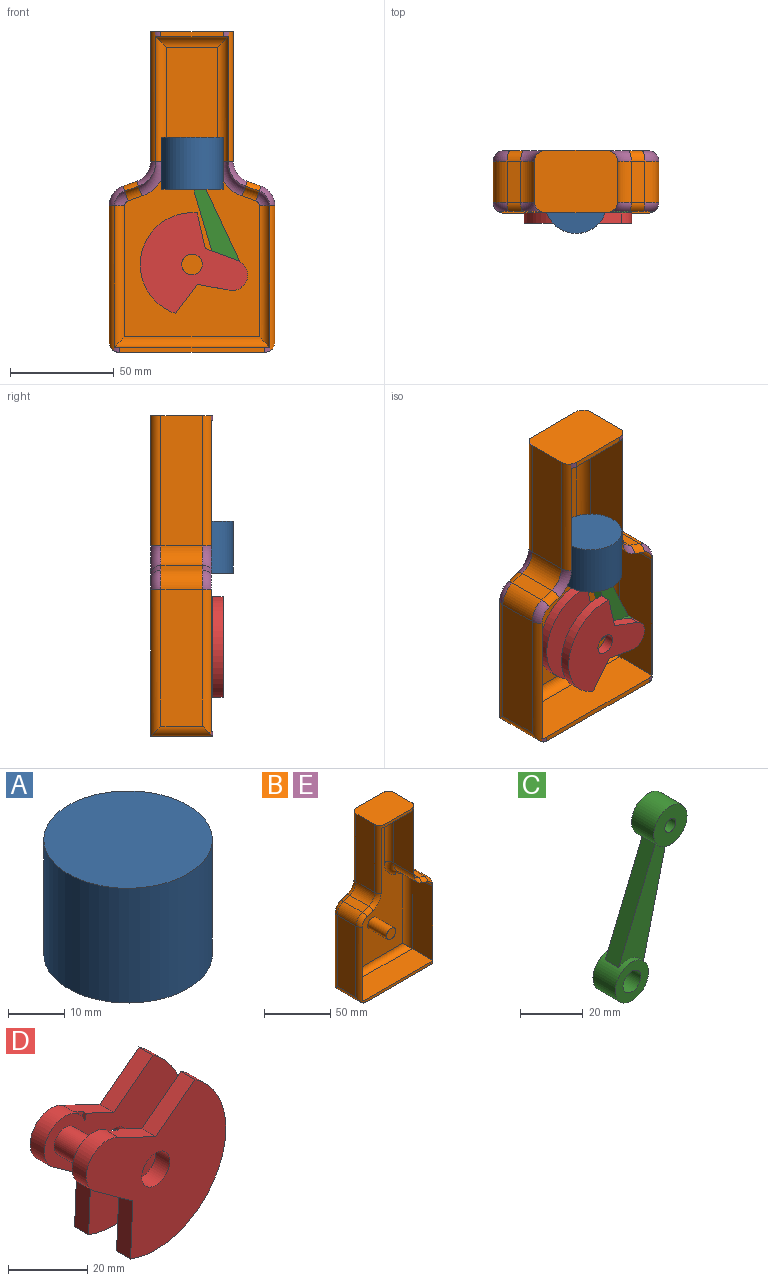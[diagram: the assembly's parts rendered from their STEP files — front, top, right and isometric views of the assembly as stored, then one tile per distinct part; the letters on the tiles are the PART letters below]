
ASSEMBLY  parts=5 mates=4
PART A: 17 faces, bbox 30x30x25 mm
  f0: cylinder r=5mm len=10mm, axis (0,1,0), area 101.5mm2, adj f1,f3,f8,f11
  f1: plane 21.82x12mm, normal (1,0,0), area 181.8mm2, adj f0,f3,f7,f9,f10,f11,f12
  f2: plane 21.82x7mm, normal (0,0,-1), area 109.8mm2, adj f3,f8
  f3: cylinder r=12mm len=24mm, axis (0,0,1), area 1330.9mm2, adj f0,f1,f2,f5,f7,f8,f9
  f4: plane 30x30mm, normal (0,0,1), area 706.9mm2, adj f6
  f5: plane 30x30mm, normal (0,0,-1), area 254.5mm2, adj f3,f6
  f6: cylinder r=15mm len=30mm, axis (0,0,1), area 2356.2mm2, adj f4,f5
  f7: plane 21.82x7mm, normal (0,0,-1), area 109.8mm2, adj f1,f3
  f8: plane 21.82x12mm, normal (-1,0,0), area 181.8mm2, adj f0,f2,f3,f9,f10,f11,f12
  f9: cylinder r=5mm len=10mm, axis (0,1,0), area 101.5mm2, adj f1,f3,f8,f12
  f10: plane 10x10mm, normal (0,0,-1), area 100mm2, adj f1,f8,f11,f12
  f11: plane 13x10mm, normal (0,-1,0), area 99.6mm2, adj f0,f1,f8,f10,f15
  f12: plane 13x10mm, normal (0,1,0), area 99.6mm2, adj f1,f8,f9,f10,f14
  f13: cylinder r=12mm len=5mm, axis (0,0,1), area 19.7mm2, adj f14
  f14: cylinder r=2.5mm len=7mm, axis (0,1,0), area 107.9mm2, adj f12,f13
  f15: cylinder r=2.5mm len=7mm, axis (0,1,0), area 107.9mm2, adj f11,f16
  f16: cylinder r=12mm len=5mm, axis (0,0,1), area 19.7mm2, adj f15
PART B: 64 faces, bbox 81.6x30x155 mm
  f0: plane 30x2.5mm, normal (0,-1,0), area 75mm2, adj f9,f23,f28,f39
  f1: cylinder r=10mm len=20mm, axis (0,1,0), area 246.5mm2, adj f2,f12,f42,f46
  f2: plane 65.88x20mm, normal (-1,0,0), area 1317.6mm2, adj f1,f43,f44,f45
  f3: plane 70x30mm, normal (0,0,-1), area 2100mm2, adj f13,f14,f33,f44
  f4: plane 65.88x20mm, normal (1,0,0), area 1317.6mm2, adj f5,f32,f33,f34
  f5: cylinder r=10mm len=20mm, axis (0,1,0), area 246.5mm2, adj f4,f6,f31,f35
  f6: plane 20x6.64mm, normal (0.33,0,0.94), area 140.7mm2, adj f5,f7,f30,f36
  f7: cylinder r=10mm len=20mm, axis (0,1,0), area 246.5mm2, adj f6,f8,f29,f37
  f8: plane 62.92x20mm, normal (1,0,0), area 1258.3mm2, adj f7,f9,f28,f38
  f9: plane 40x30mm, normal (0,0,1), area 1178.5mm2, adj f0,f8,f10,f14,f28,f38,f39,f49
  f10: plane 62.92x20mm, normal (-1,0,0), area 1258.3mm2, adj f9,f11,f39,f49
  f11: cylinder r=10mm len=20mm, axis (0,1,0), area 246.5mm2, adj f10,f12,f40,f48
  f12: plane 20x6.64mm, normal (-0.33,0,0.94), area 140.7mm2, adj f1,f11,f41,f47
  f13: plane 70x2.5mm, normal (0,-1,0), area 175mm2, adj f3,f17,f32,f43
  f14: plane 155x70mm, normal (0,1,0), area 7804.5mm2, adj f3,f9,f34,f35,f36,f37,f38,f45
  f15: cylinder r=7.5mm len=21.83mm, axis (0,1,0), area 201.8mm2, adj f16,f26,f42,f58
  f16: plane 68.38x21.83mm, normal (1,0,0), area 1492.8mm2, adj f15,f17,f43,f60
  f17: plane 75x22.5mm, normal (0,0,1), area 1686.4mm2, adj f13,f16,f18,f32,f43,f62
  f18: plane 68.38x21.83mm, normal (-1,0,0), area 1492.8mm2, adj f17,f19,f32,f63
  f19: cylinder r=7.5mm len=21.83mm, axis (0,1,0), area 201.8mm2, adj f18,f20,f31,f61
  f20: plane 21.83x6.64mm, normal (-0.33,0,-0.94), area 153.6mm2, adj f19,f21,f30,f59
  f21: cylinder r=12.5mm len=21.83mm, axis (0,1,0), area 336.3mm2, adj f20,f22,f29,f57
  f22: plane 60.42x21.83mm, normal (-1,0,0), area 1318.9mm2, adj f21,f23,f28,f55
  f23: plane 35x22.5mm, normal (0,0,-1), area 786.4mm2, adj f0,f22,f24,f28,f39,f53
  f24: plane 60.42x21.83mm, normal (1,0,0), area 1318.9mm2, adj f23,f25,f39,f52
  f25: cylinder r=12.5mm len=21.83mm, axis (0,1,0), area 336.3mm2, adj f24,f26,f40,f54
  f26: plane 21.83x6.64mm, normal (0.33,0,-0.94), area 153.6mm2, adj f15,f25,f41,f56
  f27: plane 140x65mm, normal (0,-1,0), area 6223.5mm2, adj f50,f52,f53,f54,f55,f56,f57,f58
  f28: cylinder r=5mm len=62.92mm, axis (0,0,-1), area 336mm2, adj f0,f8,f9,f22,f23,f29
  f29: torus R=15mm, axis (0,-1,0), area 70.1mm2, adj f7,f21,f28,f30
  f30: cylinder r=5mm len=7.47mm, axis (0.94,0,-0.33), area 36.8mm2, adj f6,f20,f29,f31
  f31: torus R=5mm, axis (0,-1,0), area 59mm2, adj f5,f19,f30,f32
  f32: cylinder r=5mm len=70.88mm, axis (0,0,-1), area 363.4mm2, adj f4,f13,f17,f18,f31,f33
  f33: cylinder r=5mm len=30mm, axis (0,-1,0), area 207.1mm2, adj f3,f4,f32,f34
  f34: cylinder r=5mm len=70.88mm, axis (0,0,1), area 542.4mm2, adj f4,f14,f33,f35
  f35: torus R=5mm, axis (0,-1,0), area 79.2mm2, adj f5,f14,f34,f36
  f36: cylinder r=5mm len=8.29mm, axis (-0.94,0,0.33), area 55.2mm2, adj f6,f14,f35,f37
  f37: torus R=15mm, axis (0,-1,0), area 114.4mm2, adj f7,f14,f36,f38
  f38: cylinder r=5mm len=62.92mm, axis (0,0,1), area 494.1mm2, adj f8,f9,f14,f37
  f39: cylinder r=5mm len=62.92mm, axis (0,0,1), area 336mm2, adj f0,f9,f10,f23,f24,f40
  f40: torus R=15mm, axis (0,-1,0), area 70.1mm2, adj f11,f25,f39,f41
  f41: cylinder r=5mm len=7.47mm, axis (-0.94,0,-0.33), area 36.8mm2, adj f12,f26,f40,f42
  f42: torus R=5mm, axis (0,-1,0), area 59mm2, adj f1,f15,f41,f43
  f43: cylinder r=5mm len=70.88mm, axis (0,0,1), area 363.4mm2, adj f2,f13,f16,f17,f42,f44
  f44: cylinder r=5mm len=30mm, axis (0,1,0), area 207.1mm2, adj f2,f3,f43,f45
  f45: cylinder r=5mm len=70.88mm, axis (0,0,-1), area 542.4mm2, adj f2,f14,f44,f46
  f46: torus R=5mm, axis (0,-1,0), area 79.2mm2, adj f1,f14,f45,f47
  f47: cylinder r=5mm len=8.29mm, axis (-0.94,0,-0.33), area 55.2mm2, adj f12,f14,f46,f48
  f48: torus R=15mm, axis (0,-1,0), area 114.4mm2, adj f11,f14,f47,f49
  f49: cylinder r=5mm len=62.92mm, axis (0,0,-1), area 494.1mm2, adj f9,f10,f14,f48
  f50: cylinder r=5mm len=20mm, axis (0,-1,0), area 628.3mm2, adj f27,f51
  f51: plane 10x10mm, normal (0,-1,0), area 78.5mm2, adj f50
  f52: cylinder r=5mm len=60.42mm, axis (0,0,1), area 460.2mm2, adj f24,f27,f53,f54
  f53: cylinder r=5mm len=35mm, axis (1,0,0), area 246.3mm2, adj f23,f27,f52,f55
  f54: torus R=17.5mm, axis (0,-1,0), area 138.6mm2, adj f25,f27,f52,f56
  f55: cylinder r=5mm len=60.42mm, axis (0,0,-1), area 460.2mm2, adj f22,f27,f53,f57
  f56: cylinder r=5mm len=8.29mm, axis (0.94,0,0.33), area 55.2mm2, adj f26,f27,f54,f58
  f57: torus R=17.5mm, axis (0,-1,0), area 138.6mm2, adj f21,f27,f55,f59
  f58: torus R=2.5mm, axis (0,-1,0), area 55mm2, adj f15,f27,f56,f60
  f59: cylinder r=5mm len=8.29mm, axis (0.94,0,-0.33), area 55.2mm2, adj f20,f27,f57,f61
  f60: cylinder r=5mm len=68.38mm, axis (0,0,1), area 522.8mm2, adj f16,f27,f58,f62
  f61: torus R=2.5mm, axis (0,-1,0), area 55mm2, adj f19,f27,f59,f63
  f62: cylinder r=5mm len=75mm, axis (-1,0,0), area 560.5mm2, adj f17,f27,f60,f63
  f63: cylinder r=5mm len=68.38mm, axis (0,0,-1), area 522.8mm2, adj f18,f27,f61,f62
PART C: 12 faces, bbox 32.3x10x67.2 mm
  f0: plane 39.99x16.56mm, normal (-0.92,0,0.38), area 259.7mm2, adj f8,f9,f10,f11
  f1: plane 42.04x10.31mm, normal (0.97,0,-0.24), area 259.7mm2, adj f8,f9,f10,f11
  f2: plane 15x15mm, normal (0,-1,0), area 157.1mm2, adj f7,f9
  f3: plane 15x15mm, normal (0,-1,0), area 126.4mm2, adj f6,f8
  f4: plane 15x15mm, normal (0,1,0), area 157.1mm2, adj f7,f9
  f5: plane 15x15mm, normal (0,1,0), area 126.4mm2, adj f6,f8
  f6: cylinder r=4mm len=10mm, axis (0,1,0), area 251.3mm2, adj f3,f5
  f7: cylinder r=2.5mm len=10mm, axis (0,1,0), area 157.1mm2, adj f2,f4
  f8: cylinder r=7.5mm len=15mm, axis (0,1,0), area 391.9mm2, adj f0,f1,f3,f5,f10,f11
  f9: cylinder r=7.5mm len=15mm, axis (0,1,0), area 440.7mm2, adj f0,f1,f2,f4,f10,f11
  f10: plane 43.71x21.27mm, normal (0,1,0), area 334.2mm2, adj f0,f1,f8,f9
  f11: plane 43.71x21.27mm, normal (0,-1,0), area 334.2mm2, adj f0,f1,f8,f9
PART D: 23 faces, bbox 49.8x20x45.7 mm
  f0: plane 49.82x45.72mm, normal (0,1,0), area 1300.3mm2, adj f10,f11,f12,f13,f14,f15,f16,f18
  f1: plane 49.82x45.72mm, normal (0,-1,0), area 1300.3mm2, adj f2,f3,f4,f5,f6,f7,f8,f18
  f2: plane 13.29x6.32mm, normal (0.43,0,0.9), area 69.7mm2, adj f1,f3,f4,f9,f19,f20
  f3: plane 13.98x10.72mm, normal (-0.61,0,0.79), area 88.1mm2, adj f1,f2,f8,f9
  f4: cylinder r=7.5mm len=14.51mm, axis (0,-1,0), area 120.7mm2, adj f1,f2,f5,f9,f19,f20
  f5: plane 13.48x9.63mm, normal (-0.58,0,-0.81), area 82.8mm2, adj f1,f4,f6,f9
  f6: plane 17.61x5mm, normal (-1,0,0.04), area 88.1mm2, adj f1,f5,f8,f9
  f7: cylinder r=5mm len=10mm, axis (0,-1,0), area 157.1mm2, adj f1,f9
  f8: cylinder r=25mm len=45.72mm, axis (0,-1,0), area 364.4mm2, adj f1,f3,f6,f9
  f9: plane 49.82x45.72mm, normal (0,1,0), area 1353.2mm2, adj f2,f3,f4,f5,f6,f7,f8
  f10: plane 13.98x10.72mm, normal (-0.61,0,0.79), area 88.1mm2, adj f0,f11,f16,f17
  f11: plane 13.29x6.32mm, normal (0.43,0,0.9), area 69.7mm2, adj f0,f10,f12,f17,f21,f22
  f12: cylinder r=7.5mm len=14.51mm, axis (0,1,0), area 120.7mm2, adj f0,f11,f13,f17,f21,f22
  f13: plane 13.48x9.63mm, normal (-0.58,0,-0.81), area 82.8mm2, adj f0,f12,f14,f17
  f14: plane 17.61x5mm, normal (-1,0,0.04), area 88.1mm2, adj f0,f13,f16,f17
  f15: cylinder r=5mm len=10mm, axis (0,1,0), area 157.1mm2, adj f0,f17
  f16: cylinder r=25mm len=45.72mm, axis (0,1,0), area 364.4mm2, adj f0,f10,f14,f17
  f17: plane 49.82x45.72mm, normal (0,-1,0), area 1353.2mm2, adj f10,f11,f12,f13,f14,f15,f16
  f18: cylinder r=4mm len=10mm, axis (0,1,0), area 251.3mm2, adj f0,f1
  f19: plane 3.66x3.47mm, normal (0,-1,0), area 2.7mm2, adj f2,f4,f20
  f20: plane 2.01x1mm, normal (-0.97,0,0.24), area 2.1mm2, adj f1,f2,f4,f19
  f21: plane 2.01x1mm, normal (-0.97,0,0.24), area 2.1mm2, adj f0,f11,f12,f22
  f22: plane 3.66x3.47mm, normal (0,1,0), area 2.7mm2, adj f11,f12,f21
PART E: same geometry as B
PLACE A t=(-101.26,-17.5,-63.35)mm
PLACE B t=(-101.26,7.5,2.74)mm
PLACE C rot(axis=(0,-1,0),38.9deg) t=(-101.26,-17.5,-63.35)mm
PLACE D rot(axis=(0,1,0),164.7deg) t=(-84.86,-17.5,-169.76)mm
PLACE E t=(-101.26,7.5,2.74)mm fixed
MATE revolute E.f50 <-> D.f7  axis (0,-1,0) through (-101.26,-15,-109.76)mm
MATE revolute D.f4 <-> C.f6  axis (0,1,0) through (-81.92,-17.5,-114.84)mm
MATE slider A.f3 <-> E.f9  axis (0,0,1) through (-101.26,-17.5,-48.35)mm
MATE revolute C.f7 <-> A.f0  axis (0,1,0) through (-101.26,-12.5,-63.35)mm
